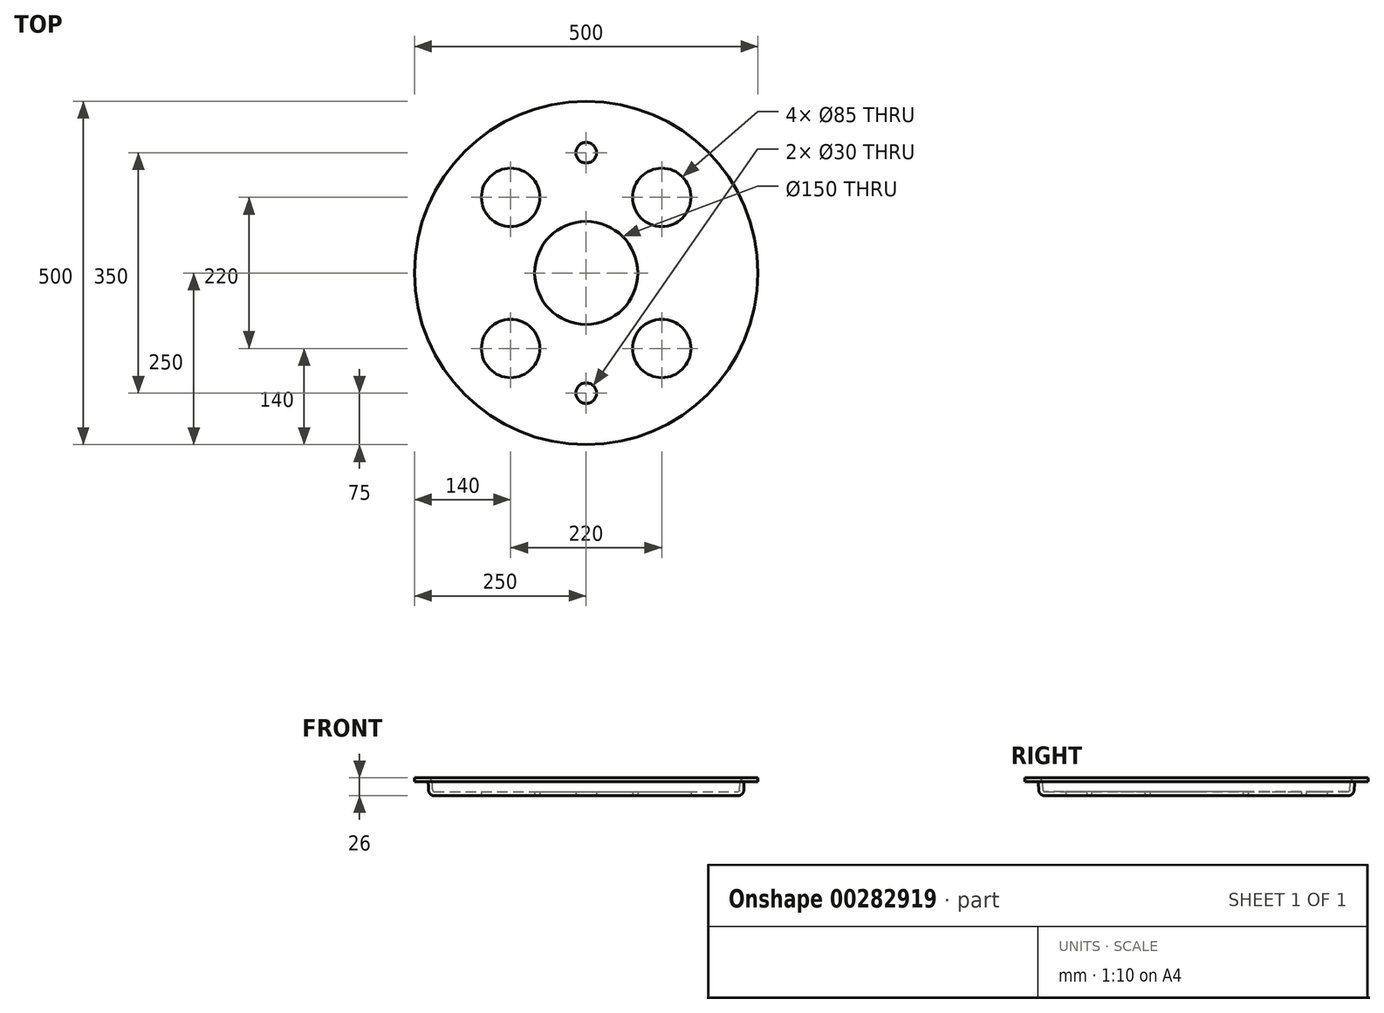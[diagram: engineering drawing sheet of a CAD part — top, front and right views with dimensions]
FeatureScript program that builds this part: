
annotation { "Feature Type Name" : "Feature", "Feature Type Description" : "" }
export const myFeature = defineFeature(function(context is Context, id is Id, definition is map)
    precondition{}
    {
        {
            var Q0;
            Q0=qCreatedBy(makeId("Front.planeOp"),FACE);
            var sketch = newSketch(context, id + "F0", { "sketchPlane" : qUnion([Q0])});
            skLineSegment(sketch, "E0", {"start": v(0, 0) * mm, "end": v(-221.36, 0) * mm});
            skLineSegment(sketch, "E1", {"start": v(-229.35, 7.58) * mm, "end": v(-229.9, 18.1) * mm});
            skLineSegment(sketch, "E2", {"start": v(-231.9, 20) * mm, "end": v(-250, 20) * mm});
            skPoint(sketch, "E3.visualSharp", {"position": v(-228.95, 0) * mm});
            skPoint(sketch, "E4.visualSharp", {"position": v(-230, 20) * mm});
            skArc(sketch, "E4.filletArc", {"start": v(-229.9, 18.1) * mm, "mid": v(-230.52, 19.45) * mm, "end": v(-231.9, 20) * mm});
            skLineSegment(sketch, "E5.0", {"start": v(-231.9, 26) * mm, "end": v(-250, 26) * mm});
            skArc(sketch, "E6.0", {"start": v(-223.9, 18.42) * mm, "mid": v(-226.4, 23.8) * mm, "end": v(-231.9, 26) * mm});
            skArc(sketch, "E7.filletArc", {"start": v(-229.35, 7.58) * mm, "mid": v(-226.87, 2.2) * mm, "end": v(-221.36, 0) * mm});
            skLineSegment(sketch, "E8.0", {"start": v(-223.36, 7.9) * mm, "end": v(-223.9, 18.42) * mm});
            skArc(sketch, "E9.0", {"start": v(-223.36, 7.9) * mm, "mid": v(-222.74, 6.55) * mm, "end": v(-221.36, 6) * mm});
            skLineSegment(sketch, "E10.0", {"start": v(0, 6) * mm, "end": v(-221.36, 6) * mm});
            skLineSegment(sketch, "E11", {"start": v(-250, 26) * mm, "end": v(-250, 20) * mm});
            skLineSegment(sketch, "E12", {"start": v(0, 0) * mm, "end": v(0, 68.02) * mm, "construction": true});
            skLineSegment(sketch, "E13", {"start": v(0, 6) * mm, "end": v(0, 0) * mm});
            skSolve(sketch);
        }
        {
            var Q0;
            Q0 = qSketchRegion(id + "F0", true);
            var Q1;
            Q1=sQuery(id+"F0.wireOp",EDGE,"E12");
            revolve(context, id + "F1", {"entities" : qUnion([Q0]), "axis" : qUnion([Q1]), "revolveType" : RevolveType.FULL});
        }
        {
            var Q0;
            Q0=qCreatedBy(makeId("Top.planeOp"),FACE);
            var sketch = newSketch(context, id + "F2", { "sketchPlane" : qUnion([Q0])});
            skLineSegment(sketch, "E14", {"start": v(0, -271.87) * mm, "end": v(0, 283.53) * mm, "construction": true});
            skLineSegment(sketch, "E15", {"start": v(-304.74, 0) * mm, "end": v(351.54, 0) * mm, "construction": true});
            skLineSegment(sketch, "E16.0", {"start": v(-110, -271.87) * mm, "end": v(-110, 283.53) * mm, "construction": true});
            skLineSegment(sketch, "E17.0", {"start": v(110, -271.87) * mm, "end": v(110, 283.53) * mm, "construction": true});
            skLineSegment(sketch, "E18.0", {"start": v(-304.74, -110) * mm, "end": v(351.54, -110) * mm, "construction": true});
            skCircle(sketch, "E19.0", {"center": v(0, 0) * mm, "radius": 216.36 * mm, "construction": true});
            skLineSegment(sketch, "E20.0", {"start": v(-304.74, 110) * mm, "end": v(351.54, 110) * mm, "construction": true});
            skCircle(sketch, "E21", {"center": v(-110, -110) * mm, "radius": 42.5 * mm});
            skCircle(sketch, "E22", {"center": v(110, -110) * mm, "radius": 42.5 * mm});
            skCircle(sketch, "E23", {"center": v(110, 110) * mm, "radius": 42.5 * mm});
            skCircle(sketch, "E24", {"center": v(-110, 110) * mm, "radius": 42.5 * mm});
            skCircle(sketch, "E25", {"center": v(0, 0) * mm, "radius": 75 * mm});
            skCircle(sketch, "E26", {"center": v(0, -175) * mm, "radius": 15 * mm});
            skCircle(sketch, "E27", {"center": v(0, 175) * mm, "radius": 15 * mm});
            skSolve(sketch);
        }
        {
            var Q0;
            Q0 = qSketchRegion(id + "F2", true);
            extrude(context, id + "F3", {"entities" : qUnion([Q0]), "operationType" : NewBodyOperationType.REMOVE, "depth" : 25 * mm});
        }
    });
